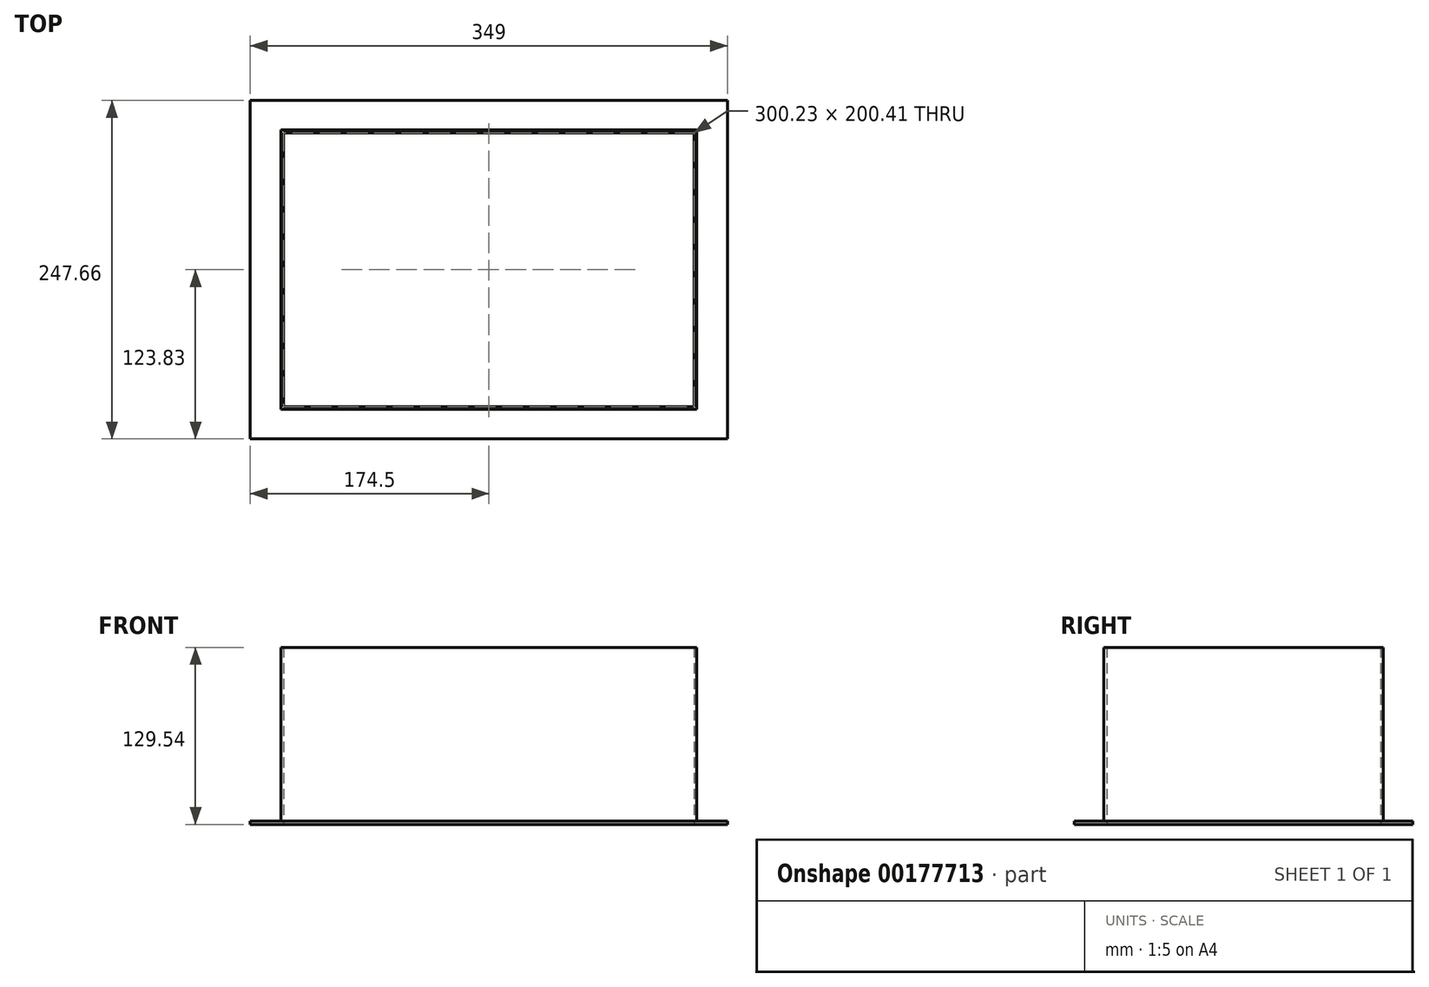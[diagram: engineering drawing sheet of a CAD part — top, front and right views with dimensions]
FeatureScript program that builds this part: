
annotation { "Feature Type Name" : "Feature", "Feature Type Description" : "" }
export const myFeature = defineFeature(function(context is Context, id is Id, definition is map)
    precondition{}
    {
        {
            var Q0;
            Q0=qCreatedBy(makeId("Top.planeOp"),FACE);
            var sketch = newSketch(context, id + "F0", { "sketchPlane" : qUnion([Q0])});
            skLineSegment(sketch, "E0.bottom", {"start": v(174.5, 123.83) * mm, "end": v(-174.5, 123.83) * mm});
            skLineSegment(sketch, "E0.top", {"start": v(174.5, -123.83) * mm, "end": v(-174.5, -123.83) * mm});
            skLineSegment(sketch, "E0.left", {"start": v(174.5, 123.83) * mm, "end": v(174.5, -123.83) * mm});
            skLineSegment(sketch, "E0.right", {"start": v(-174.5, 123.82) * mm, "end": v(-174.5, -123.82) * mm});
            skPoint(sketch, "E0.middle", {"position": v(0, 0) * mm});
            skLineSegment(sketch, "E1", {"start": v(-150.11, 100.2) * mm, "end": v(150.11, 100.2) * mm});
            skLineSegment(sketch, "E2", {"start": v(-150.11, -100.2) * mm, "end": v(150.11, -100.2) * mm});
            skLineSegment(sketch, "E3", {"start": v(-150.11, 100.2) * mm, "end": v(-150.11, -100.2) * mm});
            skLineSegment(sketch, "E4", {"start": v(150.11, 100.2) * mm, "end": v(150.11, -100.2) * mm});
            skCircle(sketch, "E5", {"center": v(162.56, -112.01) * mm, "radius": 3.81 * mm, "construction": true});
            skCircle(sketch, "E6", {"center": v(54.36, -112.01) * mm, "radius": 3.81 * mm, "construction": true});
            skCircle(sketch, "E7", {"center": v(-54.1, -112.01) * mm, "radius": 3.81 * mm, "construction": true});
            skCircle(sketch, "E8", {"center": v(-163.83, -112.01) * mm, "radius": 3.81 * mm, "construction": true});
            skCircle(sketch, "E9", {"center": v(-163.83, -1.27) * mm, "radius": 3.81 * mm, "construction": true});
            skCircle(sketch, "E10", {"center": v(-163.83, 109.47) * mm, "radius": 3.81 * mm, "construction": true});
            skCircle(sketch, "E11", {"center": v(-54.1, 109.47) * mm, "radius": 3.81 * mm, "construction": true});
            skCircle(sketch, "E12", {"center": v(54.36, 109.47) * mm, "radius": 3.81 * mm, "construction": true});
            skCircle(sketch, "E13", {"center": v(162.56, 109.47) * mm, "radius": 3.81 * mm, "construction": true});
            skCircle(sketch, "E14", {"center": v(162.56, -1.27) * mm, "radius": 3.81 * mm, "construction": true});
            skSolve(sketch);
        }
        {
            var Q0;
            Q0=qSketchRegion(id+"F0",true);
            extrude(context, id + "F1", {"entities" : qUnion([Q0]), "depth" : 2.54 * mm});
        }
        {
            var Q0;
            Q0=makeQuery(id+"F1.opExtrude","CAP_FACE",FACE,{"disambiguationData":[OSD([sQuery(id+"F0.wireOp",EDGE,"E0.bottom"),sQuery(id+"F0.wireOp",EDGE,"E0.top"),sQuery(id+"F0.wireOp",EDGE,"E0.left"),sQuery(id+"F0.wireOp",EDGE,"E0.right"),sQuery(id+"F0.wireOp",EDGE,"E1"),sQuery(id+"F0.wireOp",EDGE,"E2"),sQuery(id+"F0.wireOp",EDGE,"E3"),sQuery(id+"F0.wireOp",EDGE,"E4"),sQuery(id+"F0.wireOp",EDGE,"E5"),sQuery(id+"F0.wireOp",EDGE,"E6"),sQuery(id+"F0.wireOp",EDGE,"E7"),sQuery(id+"F0.wireOp",EDGE,"E8"),sQuery(id+"F0.wireOp",EDGE,"E9"),sQuery(id+"F0.wireOp",EDGE,"E10"),sQuery(id+"F0.wireOp",EDGE,"E11"),sQuery(id+"F0.wireOp",EDGE,"E12"),sQuery(id+"F0.wireOp",EDGE,"E13"),sQuery(id+"F0.wireOp",EDGE,"E14")])],"isStart":false});
            var sketch = newSketch(context, id + "F2", { "sketchPlane" : qUnion([Q0])});
            skLineSegment(sketch, "E15.0", {"start": v(-152.15, 102.24) * mm, "end": v(-152.15, -102.23) * mm});
            skLineSegment(sketch, "E15.1", {"start": v(-152.15, 102.24) * mm, "end": v(152.15, 102.24) * mm});
            skLineSegment(sketch, "E15.2", {"start": v(152.15, 102.24) * mm, "end": v(152.15, -102.23) * mm});
            skLineSegment(sketch, "E15.3", {"start": v(-152.15, -102.23) * mm, "end": v(152.15, -102.23) * mm});
            skLineSegment(sketch, "E16.0", {"start": v(-150.11, 100.2) * mm, "end": v(-150.11, -100.2) * mm});
            skLineSegment(sketch, "E16.1", {"start": v(-150.11, 100.2) * mm, "end": v(150.11, 100.2) * mm});
            skLineSegment(sketch, "E16.2", {"start": v(150.11, 100.2) * mm, "end": v(150.11, -100.2) * mm});
            skLineSegment(sketch, "E16.3", {"start": v(-150.11, -100.2) * mm, "end": v(150.11, -100.2) * mm});
            skSolve(sketch);
        }
        {
            var Q0;
            Q0=qSketchRegion(id+"F2",true);
            extrude(context, id + "F3", {"entities" : qUnion([Q0]), "operationType" : NewBodyOperationType.ADD, "depth" : 127 * mm});
        }
    });
